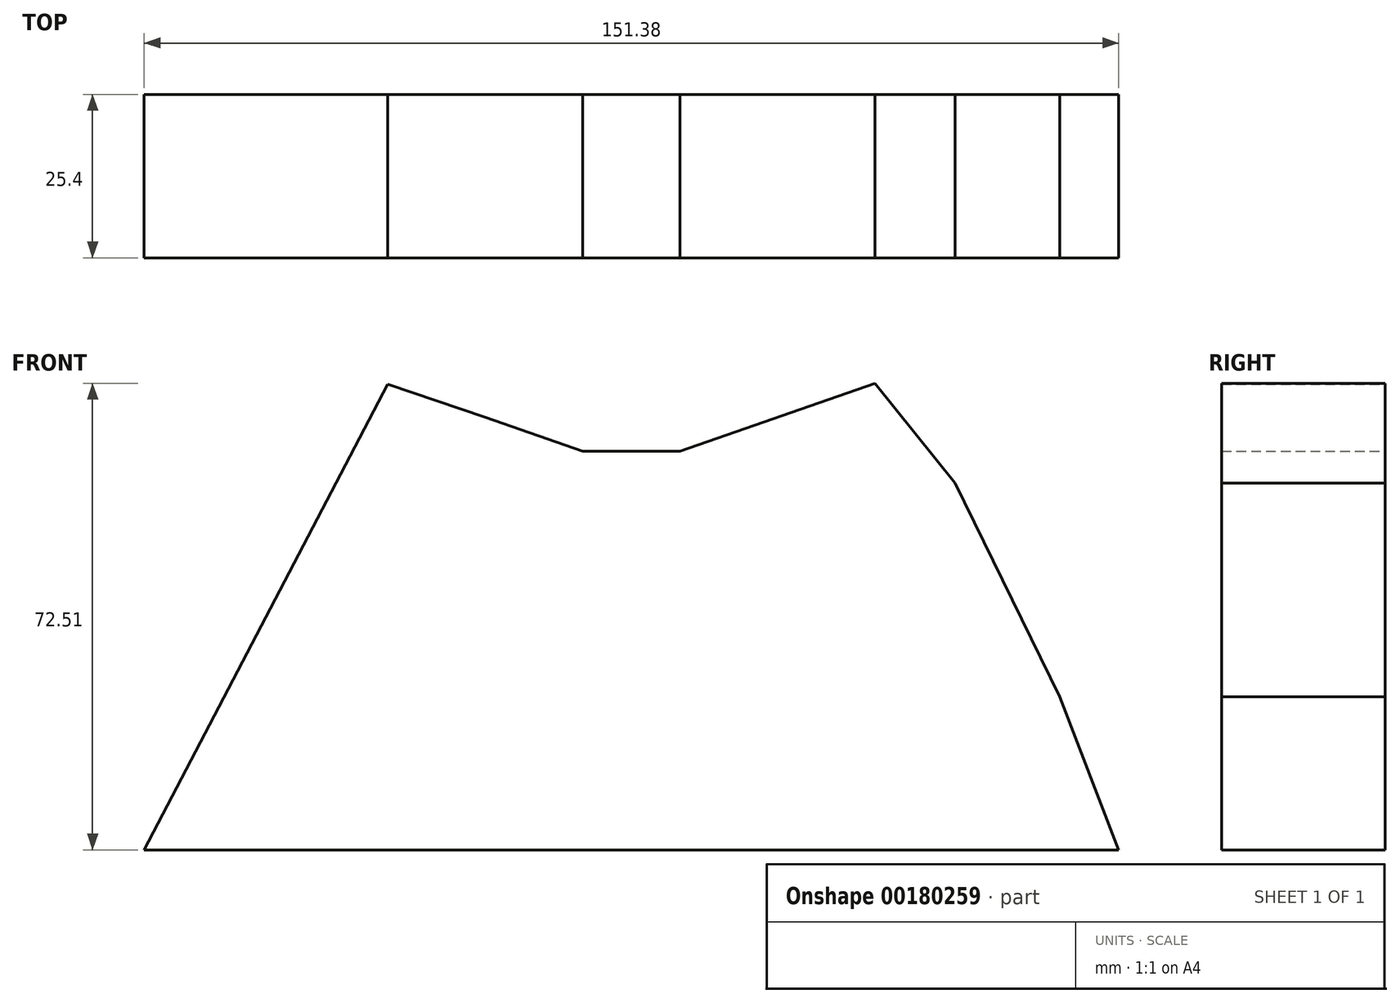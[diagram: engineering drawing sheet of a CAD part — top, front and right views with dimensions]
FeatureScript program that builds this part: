
annotation { "Feature Type Name" : "Feature", "Feature Type Description" : "" }
export const myFeature = defineFeature(function(context is Context, id is Id, definition is map)
    precondition{}
    {
        {
            var Q0;
            Q0=qCreatedBy(makeId("Front.planeOp"),FACE);
            var sketch = newSketch(context, id + "F0", { "sketchPlane" : qUnion([Q0])});
            skLineSegment(sketch, "E0", {"start": v(-76.05, 0) * mm, "end": v(75.33, 0) * mm});
            skLineSegment(sketch, "E1", {"start": v(75.33, 0) * mm, "end": v(66.19, 0) * mm});
            skLineSegment(sketch, "E2", {"start": v(75.33, 0) * mm, "end": v(37.49, 0) * mm});
            skLineSegment(sketch, "E3", {"start": v(-38.2, 0) * mm, "end": v(37.49, 0) * mm});
            skLineSegment(sketch, "E4", {"start": v(-38.2, 0) * mm, "end": v(-38.2, 76.2) * mm});
            skLineSegment(sketch, "E5", {"start": v(37.49, 0) * mm, "end": v(37.49, 76.2) * mm});
            skLineSegment(sketch, "E6", {"start": v(-38.2, 0) * mm, "end": v(-29.39, 0) * mm});
            skLineSegment(sketch, "E7", {"start": v(-38.2, 0) * mm, "end": v(-23.07, 0) * mm});
            skLineSegment(sketch, "E8", {"start": v(-23.07, 0) * mm, "end": v(-23.07, 67.24) * mm});
            skLineSegment(sketch, "E9", {"start": v(37.49, 0) * mm, "end": v(22.35, 0) * mm});
            skLineSegment(sketch, "E10", {"start": v(22.35, 0) * mm, "end": v(22.35, 67.24) * mm});
            skLineSegment(sketch, "E11", {"start": v(-23.07, 0) * mm, "end": v(-7.93, 0) * mm});
            skLineSegment(sketch, "E12", {"start": v(22.35, 0) * mm, "end": v(7.2, 0) * mm});
            skLineSegment(sketch, "E13", {"start": v(7.2, 0) * mm, "end": v(-7.93, 0) * mm});
            skLineSegment(sketch, "E14", {"start": v(7.2, 0) * mm, "end": v(2.16, 0) * mm});
            skLineSegment(sketch, "E15", {"start": v(-23.07, 67.24) * mm, "end": v(-38.2, 72.37) * mm});
            skLineSegment(sketch, "E16", {"start": v(22.35, 67.24) * mm, "end": v(37.49, 72.5) * mm});
            skLineSegment(sketch, "E17", {"start": v(22.35, 67.24) * mm, "end": v(7.2, 61.98) * mm});
            skLineSegment(sketch, "E18", {"start": v(7.2, 61.98) * mm, "end": v(-7.93, 61.98) * mm});
            skLineSegment(sketch, "E19", {"start": v(-7.93, 61.98) * mm, "end": v(-23.07, 67.24) * mm});
            skLineSegment(sketch, "E20", {"start": v(-7.93, 61.98) * mm, "end": v(-7.93, 0) * mm});
            skLineSegment(sketch, "E21", {"start": v(7.2, 61.98) * mm, "end": v(7.2, 0) * mm});
            skLineSegment(sketch, "E22", {"start": v(-76.05, 0) * mm, "end": v(-63.6, 0) * mm});
            skLineSegment(sketch, "E23", {"start": v(-63.6, 0) * mm, "end": v(-46.24, 0) * mm});
            skLineSegment(sketch, "E24", {"start": v(-46.24, 0) * mm, "end": v(-38.71, 0) * mm});
            skLineSegment(sketch, "E25", {"start": v(-41.85, 72.37) * mm, "end": v(-41.85, 76.2) * mm});
            skLineSegment(sketch, "E26", {"start": v(-46.24, 0) * mm, "end": v(-46.24, 57.02) * mm});
            skLineSegment(sketch, "E27", {"start": v(-63.6, 0) * mm, "end": v(-63.6, 23.8) * mm});
            skLineSegment(sketch, "E28", {"start": v(37.49, 0) * mm, "end": v(49.93, 0) * mm});
            skLineSegment(sketch, "E29", {"start": v(49.93, 0) * mm, "end": v(49.93, 57.02) * mm});
            skLineSegment(sketch, "E30", {"start": v(66.19, 0) * mm, "end": v(66.19, 23.8) * mm});
            skLineSegment(sketch, "E31", {"start": v(37.49, 72.5) * mm, "end": v(49.93, 57.02) * mm});
            skLineSegment(sketch, "E32", {"start": v(49.93, 57.02) * mm, "end": v(66.19, 23.8) * mm});
            skLineSegment(sketch, "E33", {"start": v(66.19, 23.8) * mm, "end": v(75.33, 0) * mm});
            skLineSegment(sketch, "E34", {"start": v(-38.2, 72.37) * mm, "end": v(-46.24, 57.02) * mm});
            skLineSegment(sketch, "E35", {"start": v(-46.24, 57.02) * mm, "end": v(-63.6, 23.8) * mm});
            skLineSegment(sketch, "E36", {"start": v(-63.6, 23.8) * mm, "end": v(-76.05, 0) * mm});
            skLineSegment(sketch, "E37", {"start": v(-7.93, 61.02) * mm, "end": v(-23.07, 61.02) * mm});
            skLineSegment(sketch, "E38", {"start": v(74.46, 2.26) * mm, "end": v(-74.87, 2.26) * mm});
            skSolve(sketch);
        }
        {
            var Q0;
            Q0 = qSketchRegion(id + "F0", true);
            var Q1;
            {var subQ0=sQuery(id+"F0.wireOp",EDGE,"E37");Q1=makeQuery(id+"F0.imprint","IMPRINT",FACE,{"disambiguationData":[TD([[makeQuery(id+"F0.imprint","IMPRINT",EDGE,{"derivedFrom":subQ0}),1.0]])]});}
            extrude(context, id + "F1", {"entities" : qUnion([Q0, Q1]), "depth" : 25.4 * mm});
        }
    });
